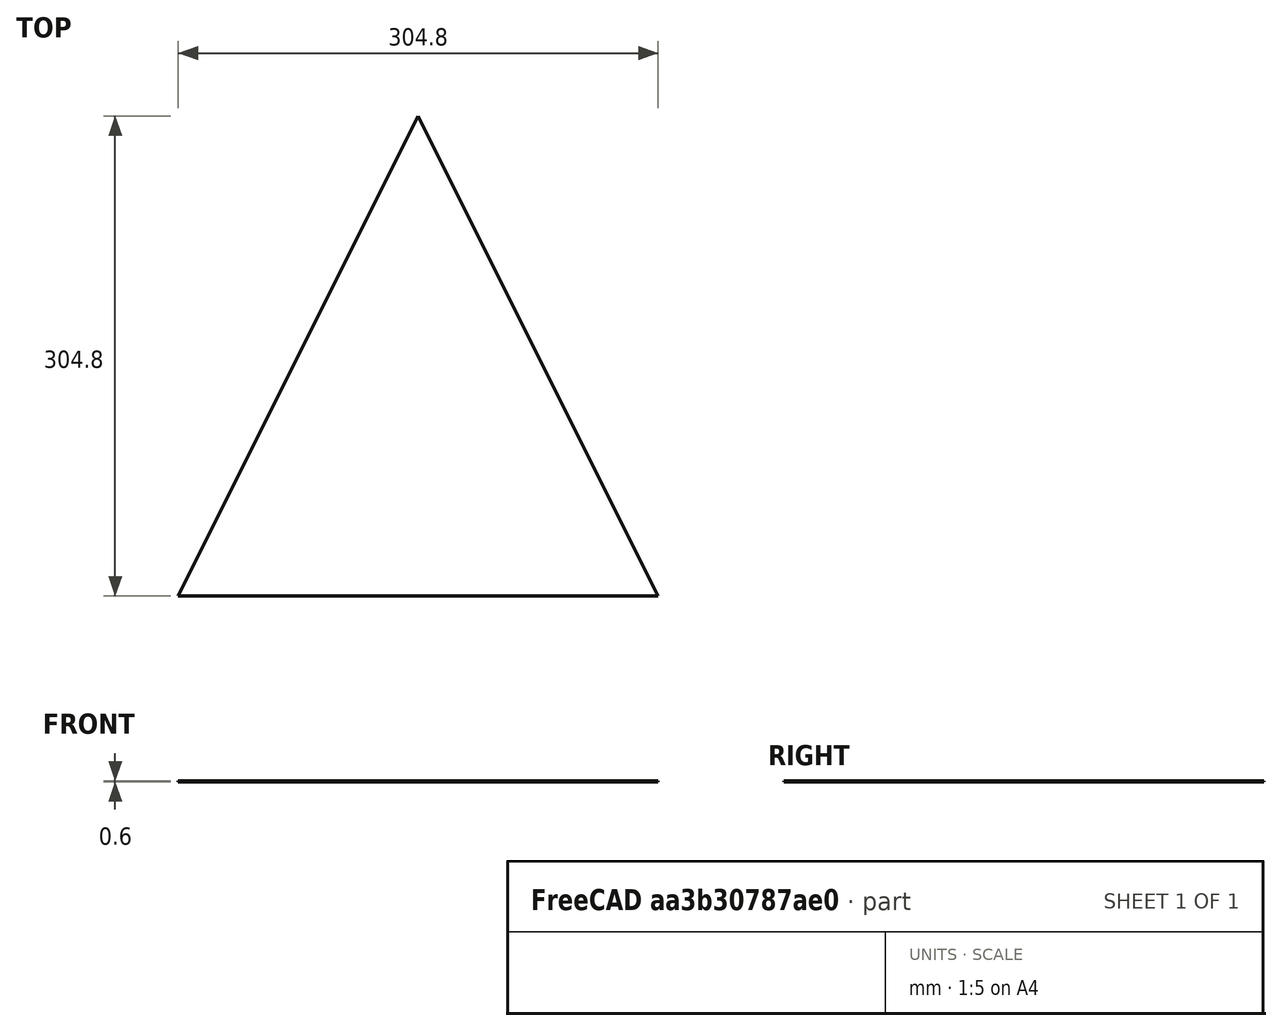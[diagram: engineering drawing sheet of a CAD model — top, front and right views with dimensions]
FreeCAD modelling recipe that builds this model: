
FCSTD DOCUMENT  (FreeCAD 0.19R22411 (Git))
Label: body
License: All rights reserved
LicenseURL: http://en.wikipedia.org/wiki/All_rights_reserved
objects: Sketcher::SketchObject×1, PartDesign::Pad×1, PartDesign::Body×1
note: 4 computed .brp shape members not serialized (recipe doc carries the construction recipe); baked Part::Feature solids carry a one-line shape summary decoded from their .brp

FEATURE [Sketcher::SketchObject] Sketch
  MapMode = 5
  Support = -> [XY_Plane]
  sketch-geometry (4):
    g0: LineSegment StartX=-152.4 StartY=0 StartZ=0 EndX=0 EndY=304.8 EndZ=0
    g1: LineSegment StartX=-2.1e-15 StartY=304.8 StartZ=0 EndX=152.4 EndY=0 EndZ=0
    g2: LineSegment StartX=152.4 StartY=0 StartZ=0 EndX=0 EndY=0 EndZ=0
    g3: LineSegment StartX=-152.4 StartY=0 StartZ=0 EndX=0 EndY=0 EndZ=0
  constraints (11):
    c: Horizontal(g2)
    c: Horizontal(g3)
    c: Equal(g0,g1)
    c: Coincident(g0,g3)
    c: Coincident(g3,g-1)
    c: Equal(g3,g2)
    c: Coincident(g0,g1)
    c: Coincident(g1,g2)
    c: Coincident(g2,g3)
    c: DistanceY(g2,g0) = 304.8
    c: DistanceX(g0,g1) = 304.8
FEATURE [PartDesign::Pad] Pad
  AllowMultiFace = false
  Length = 0.6
  Length2 = 100
  Profile = -> Sketch
  Type = 0
FEATURE [PartDesign::Body] Body
  Group = -> [Sketch,Pad]
  Origin = -> Origin
  Tip = -> Pad
